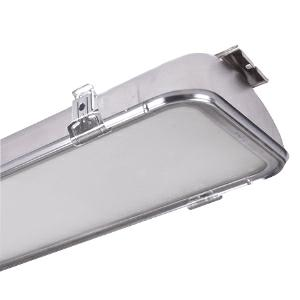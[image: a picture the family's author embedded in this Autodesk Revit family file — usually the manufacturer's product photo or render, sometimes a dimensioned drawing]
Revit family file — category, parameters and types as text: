
# Revit family: 3f_filippi_-_beta_235_93_vs_iperconcentrato_3f_filippi_-_52883_-_beta_235_led_932x40_iperconc_vs_l1265
name_source: partatom
category: Lighting Fixtures
units: mm (PartAtom-declared; Revit-internal decimal feet)

## family parameters
Cut with Voids When Loaded = No
Host = Face
Light Source = No
Part Type = Normal
Room Calculation Point = No
Round Connector Dimension = Use Diameter
Shared = No

## types (1)
- 3F Filippi - Beta 235 93 VS Iperconcentrato (1 x LED, 10985 lm, 80 W, 4000 K)
    Apparent Load = 80 VA
    Approval mark = CE
    CIE Flux Codes = 79 94 99 100 100
    Color Rendering = 80
    Color Temperature = 4000 K
    Control Gear = Electronic ballast
    Default Elevation = 1800 mm
    Description = ILLUMINOTECHNICAL
Luminous efficiency 100% (DLOR 100%, ULOR 0%).
Initial luminous flux of the luminaire 10985 lm.
Symmetrical elliptical hyperconcentrated distribution.
Installation Interdistance Transv.D = 0.51 x hu - Long.D = 0.68 x hu.
Tabular UGR (CIE 117 - 4H-8H; S=0.25H; 70/50/20): RUG 18 - 19.7.
Beam angle: 32° - 44°.
Luminous efficacy 137 lm/W.
Lifetime (L93/B10): 30000 h. (tq+25°C)
Lifetime (L90/B10): 50000 h. (tq+25°C)
Lifetime (L85/B10): 80000 h. (tq+25°C)
Lifetime (L80/B10): 100000 h. (tq+25°C)
Lifetime (L85/B10): 50000 h. (tq+45°C)
Sudden decreased luminous flux after 50000 hours: 0% (C0).
Photobiological safety in compliance with IEC/TR 62778: RG0 risk exempt, (IEC 62471).
In compliance with IEC/EN 62722-2-1 - IEC/EN 62717 standards.

SOURCE
2 linear LED modules 40W/840.
Energy efficiency class (UE 2019/2020 - UE 2019/2015): C.
CIE 13.3 Colour rendering index: CRI >80 (R9 <50%).
IES TM-30 Fidelity Index: Rf = 84 Rg = 95.
CCT nominal colour temperature 4000 K.
Colour initial tolerance (MacAdam): SDCM 3.

MECHANICAL
Housing in AISI 304 stainless steel, pressed in one single piece.
VS moulded anti-glare glass, non-combustible, single-piece perimeter frame in stainless steel.
Oversized gear-tray reflector unit in highly reflective white painted hot-galvanised steel.
Methacrylate (PMMA) lenses with external flat surface.
Stainless steel snap-lock clips for diffuser mounting (safety n° 4 per fixture).
Luminaire with limited surface temperature. - D - (EN 60598-2-24)
Dimensions: 1265x235 mm, height 105 mm. Weight 10.05 kg.
IP65 protection degree.
Mechanical strength to impacts IK09 (10 joule).
Glow-wire test resistance 960°C.

ELECTRICAL
Halogen Free electronic wiring 230V-50/60Hz, power factor 0.95, THD <25%, constant output current, class I, 1 driver.
Power of the luminaire 80 W.
ENEC - CE.
Flicker: <4%.
Luminaire compliant with EN 60598-2-22 for power supply from a centralised emergency system CPSS (Central Power Supply System), not incorporated in the luminaire - high risk areas excluded. The default power and flux are 100% in AC and 100% in DC.
Ambient temperature from -20°C to +45°C.
Temperature class T6 max 85°C.
Quick connection via M20 3P connector with 9-13 mm tightening range.
Relative humidity UR: <85%.

INSTALLATION
Ceiling / Suspended / Wall.
Recommended minimum installation height: 4 metres from the ground.
All accessories dedicated to this product are available on the Catalog and on our website www.3F-Filippi.com.

APPLICATIONS
Dry, dusty indoor environments, subject to occasional water splashes.
Any environments except the ones where the luminaire materials are unsuitable.
Industrial environments, warehouses, environments where security locks are required on all clips, e.g. prisons (on request).
Environments in which it is necessary a total protection against falling fragments (eg environments with foodstuffs or machines with moving parts or with extreme temperature changes), use luminaires with laminated glass.
Tempered glass is not immune to falling fragments from harmless and caused by shocks or exceptionally derived from the tempering process.

WARNING
Fixture not suitable for cold stores with an ambient temperature <0°C and/or relative humidity >85%.
Luminaire designed for disposal/recycling at end-of-life.
Replaceable (LED only) light source by a professional. Replaceable control gear by a professional.
    Height = 105 mm
    Lamp = 1 x LED
    Lamp Light Flux = 10985 lm
    Lamp Power = 80 W
    Lamp count = 1
    Length = 1265 mm
    Lifetime = 50000 h
    Luminous efficacy = 137 lm/W
    Manufacturer = 3F Filippi
    ModVariant = No
    Model = 3F Filippi - 52883 - Beta 235 LED 932x40 IPERCONC VS L1265
    Mounting Place = Ceiling
    Mounting Type = Pendant
    Number of Poles = 1
    OnlyDefault = Yes
    Power Factor = 1
    Product Name = 3F Filippi - Beta 235 93 VS Iperconcentrato
    Product group = pendant luminaire
    ProductGroupID = 9
    Protection Class = Protection class I
    Protection Degree = IP 65
    RLX_Detail_Level = 1
    RLX_Emergency_Light_Flux = 0 lm
    RLX_Emergency_Type = 0
    RLX_Emergency_Type_DB = No
    RlxData = <blob elided: 83957 chars, md5=1f6808fb>
    Socket = socket
    Standby Power = 0 W
    System Light Flux = 10985 lm
    System Power = 80 W
    Type Comments = Product without accessories
    Type Image = 3ffilippi_52883.jpg
    URL = http://relux.com
    VarID = ---
    Voltage = 0 V
    Weight = 0.00 kg
    Width = 235 mm

## geometry (parser evidence)
native form markers: Blend x4, Sweep x11
no freeform markers — native parametric forms only
